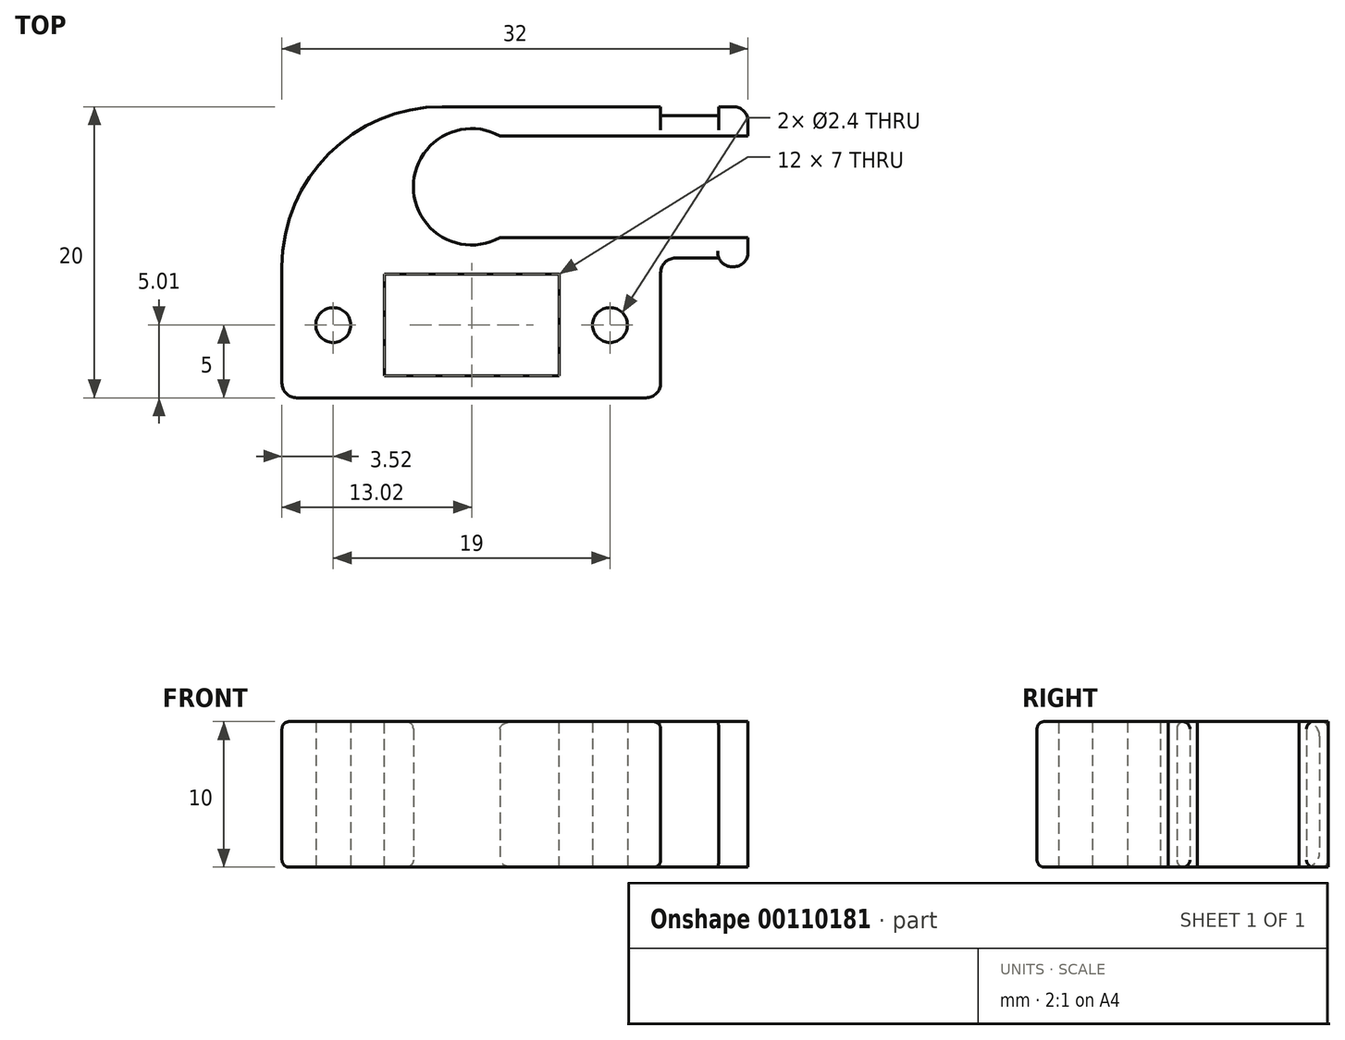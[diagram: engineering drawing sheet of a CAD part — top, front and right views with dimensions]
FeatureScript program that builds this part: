
annotation { "Feature Type Name" : "Feature", "Feature Type Description" : "" }
export const myFeature = defineFeature(function(context is Context, id is Id, definition is map)
    precondition{}
    {
        {
            var Q0;
            Q0=qCreatedBy(makeId("Top.planeOp"),FACE);
            var sketch = newSketch(context, id + "F0", { "sketchPlane" : qUnion([Q0])});
            skArc(sketch, "E0", {"start": v(-3.5, 1.94) * mm, "mid": v(-2.83, -2.83) * mm, "end": v(1.94, -3.5) * mm});
            skLineSegment(sketch, "E1.right", {"start": v(12.98, -5.5) * mm, "end": v(12.98, -14.5) * mm});
            skLineSegment(sketch, "E2.left", {"start": v(12.98, -14.5) * mm, "end": v(12.98, -5.5) * mm});
            skLineSegment(sketch, "E2.right", {"start": v(-13.02, -14.5) * mm, "end": v(-13.02, -4.5) * mm});
            skLineSegment(sketch, "E3", {"start": v(-13.02, -14.5) * mm, "end": v(12.98, -14.5) * mm});
            skLineSegment(sketch, "E4.bottom", {"start": v(-13.02, -14.5) * mm, "end": v(12.98, -14.5) * mm, "construction": true});
            skLineSegment(sketch, "E4.left", {"start": v(-13.02, -14.5) * mm, "end": v(-13.02, -9.5) * mm, "construction": true});
            skLineSegment(sketch, "E4.right", {"start": v(12.98, -14.5) * mm, "end": v(12.98, -9.7) * mm, "construction": true});
            skCircle(sketch, "E5", {"center": v(-9.5, -9.5) * mm, "radius": 1.2 * mm});
            skCircle(sketch, "E6", {"center": v(9.5, -9.5) * mm, "radius": 1.2 * mm});
            skArc(sketch, "E7", {"start": v(1.94, 3.5) * mm, "mid": v(-1.1, 3.84) * mm, "end": v(-3.5, 1.94) * mm});
            skLineSegment(sketch, "E8.top", {"start": v(-13.02, 5.5) * mm, "end": v(12.98, 5.5) * mm});
            skLineSegment(sketch, "E8.left", {"start": v(-13.02, -4.5) * mm, "end": v(-13.02, 5.5) * mm});
            skLineSegment(sketch, "E9.bottom", {"start": v(1.94, -3.5) * mm, "end": v(18.98, -3.5) * mm});
            skLineSegment(sketch, "E9.top", {"start": v(1.94, 3.5) * mm, "end": v(18.98, 3.5) * mm});
            skPoint(sketch, "E10.orphan", {"position": v(0, -3.5) * mm});
            skLineSegment(sketch, "E11.top", {"start": v(16.98, 5.5) * mm, "end": v(18.98, 5.5) * mm});
            skLineSegment(sketch, "E11.right", {"start": v(18.98, -5.5) * mm, "end": v(18.98, -3.5) * mm});
            skLineSegment(sketch, "E12.bottom", {"start": v(18.98, -3.5) * mm, "end": v(12.98, -3.5) * mm});
            skLineSegment(sketch, "E12.top", {"start": v(18.98, -5.5) * mm, "end": v(16.98, -5.5) * mm});
            skLineSegment(sketch, "E12.left", {"start": v(18.98, -3.5) * mm, "end": v(18.98, -5.5) * mm});
            skPoint(sketch, "E13.orphan", {"position": v(12.98, -4.9) * mm});
            skLineSegment(sketch, "E14.trimOffspring", {"start": v(18.98, 3.5) * mm, "end": v(18.98, 5.5) * mm});
            skPoint(sketch, "E15.orphan", {"position": v(0, -9.5) * mm});
            skLineSegment(sketch, "E16.top", {"start": v(12.98, -4.9) * mm, "end": v(16.98, -4.9) * mm});
            skLineSegment(sketch, "E16.left", {"start": v(12.98, -5.5) * mm, "end": v(12.98, -4.9) * mm});
            skLineSegment(sketch, "E16.right", {"start": v(16.98, -5.5) * mm, "end": v(16.98, -4.9) * mm});
            skLineSegment(sketch, "E17.top", {"start": v(12.98, 4.9) * mm, "end": v(16.98, 4.9) * mm});
            skLineSegment(sketch, "E17.left", {"start": v(12.98, 5.5) * mm, "end": v(12.98, 4.9) * mm});
            skLineSegment(sketch, "E17.right", {"start": v(16.98, 5.5) * mm, "end": v(16.98, 4.9) * mm});
            skSolve(sketch);
        }
        {
            var Q0;
            Q0 = qSketchRegion(id + "F0", true);
            extrude(context, id + "F1", {"entities" : qUnion([Q0]), "depth" : 10 * mm});
        }
        {
            var Q0;
            Q0=makeQuery(id+"F1.opExtrude","SWEPT_EDGE",EDGE,{"disambiguationData":[OSD([sQuery(id+"F0.wireOp",EDGE,"E11.top"),sQuery(id+"F0.wireOp",EDGE,"E14.trimOffspring")])]});
            var Q1;
            Q1=makeQuery(id+"F1.opExtrude","SWEPT_EDGE",EDGE,{"disambiguationData":[OSD([sQuery(id+"F0.wireOp",EDGE,"E12.top"),sQuery(id+"F0.wireOp",EDGE,"E12.left")])]});
            var Q2;
            Q2=makeQuery(id+"F1.opExtrude","CAP_EDGE",EDGE,{"disambiguationData":[OSD([sQuery(id+"F0.wireOp",EDGE,"E17.top")])],"isStart":false});
            var Q3;
            Q3=makeQuery(id+"F1.opExtrude","CAP_EDGE",EDGE,{"disambiguationData":[OSD([sQuery(id+"F0.wireOp",EDGE,"E17.top")])],"isStart":true});
            var Q4;
            Q4=makeQuery(id+"F1.opExtrude","SWEPT_EDGE",EDGE,{"disambiguationData":[OSD([sQuery(id+"F0.wireOp",EDGE,"E16.top"),sQuery(id+"F0.wireOp",EDGE,"E16.left")])]});
            var Q5;
            Q5=makeQuery(id+"F1.opExtrude","SWEPT_EDGE",EDGE,{"disambiguationData":[OSD([sQuery(id+"F0.wireOp",EDGE,"E3"),sQuery(id+"F0.wireOp",EDGE,"E2.left")])]});
            var Q6;
            Q6=makeQuery(id+"F1.opExtrude","SWEPT_EDGE",EDGE,{"disambiguationData":[OSD([sQuery(id+"F0.wireOp",EDGE,"E2.right"),sQuery(id+"F0.wireOp",EDGE,"E3")])]});
            fillet(context, id + "F2", {"entities" : qUnion([Q0, Q1, Q2, Q3, Q4, Q5, Q6]), "radius" : 1 * mm, "tangentPropagation" : true, "allowEdgeOverflow" : false});
        }
        {
            var Q0;
            Q0=makeQuery(id+"F1.opExtrude","SWEPT_EDGE",EDGE,{"disambiguationData":[OSD([sQuery(id+"F0.wireOp",EDGE,"E8.top"),sQuery(id+"F0.wireOp",EDGE,"E8.left")])]});
            fillet(context, id + "F3", {"entities" : qUnion([Q0]), "radius" : 11 * mm, "tangentPropagation" : true, "allowEdgeOverflow" : false});
        }
        {
            var Q0;
            Q0=makeQuery(id+"F1.opExtrude","CAP_FACE",FACE,{"disambiguationData":[OSD([sQuery(id+"F0.wireOp",EDGE,"E0"),sQuery(id+"F0.wireOp",EDGE,"E2.right"),sQuery(id+"F0.wireOp",EDGE,"E3"),sQuery(id+"F0.wireOp",EDGE,"E5"),sQuery(id+"F0.wireOp",EDGE,"E6"),sQuery(id+"F0.wireOp",EDGE,"E7"),sQuery(id+"F0.wireOp",EDGE,"E8.top"),sQuery(id+"F0.wireOp",EDGE,"E8.left"),sQuery(id+"F0.wireOp",EDGE,"E9.bottom"),sQuery(id+"F0.wireOp",EDGE,"E9.top"),sQuery(id+"F0.wireOp",EDGE,"E11.top"),sQuery(id+"F0.wireOp",EDGE,"E2.left"),sQuery(id+"F0.wireOp",EDGE,"E12.bottom"),sQuery(id+"F0.wireOp",EDGE,"E12.top"),sQuery(id+"F0.wireOp",EDGE,"E12.left"),sQuery(id+"F0.wireOp",EDGE,"E14.trimOffspring"),sQuery(id+"F0.wireOp",EDGE,"E16.top"),sQuery(id+"F0.wireOp",EDGE,"E16.left"),sQuery(id+"F0.wireOp",EDGE,"E16.right"),sQuery(id+"F0.wireOp",EDGE,"E17.top"),sQuery(id+"F0.wireOp",EDGE,"E17.left"),sQuery(id+"F0.wireOp",EDGE,"E17.right")])],"isStart":false});
            var sketch = newSketch(context, id + "F4", { "sketchPlane" : qUnion([Q0])});
            skLineSegment(sketch, "E18.bottom", {"start": v(6, -13) * mm, "end": v(-6, -13) * mm});
            skLineSegment(sketch, "E18.top", {"start": v(6, -6) * mm, "end": v(-6, -6) * mm});
            skLineSegment(sketch, "E18.left", {"start": v(6, -13) * mm, "end": v(6, -6) * mm});
            skLineSegment(sketch, "E18.right", {"start": v(-6, -13) * mm, "end": v(-6, -6) * mm});
            skPoint(sketch, "E18.middle", {"position": v(0, -9.5) * mm});
            skSolve(sketch);
        }
        {
            var Q0;
            Q0=makeQuery(id+"F4.imprint","IMPRINT",FACE,{"disambiguationData":[TD([[makeQuery(id+"F4.imprint","IMPRINT",EDGE,{"derivedFrom":sQuery(id+"F4.wireOp",EDGE,"E18.bottom")}),-1.0]])]});
            extrude(context, id + "F5", {"entities" : qUnion([Q0]), "operationType" : NewBodyOperationType.REMOVE, "oppositeDirection" : true, "depth" : 10 * mm});
        }
        {
            var Q0;
            {var subQ0=sQuery(id+"F0.wireOp",EDGE,"E8.left");var subQ1=sQuery(id+"F0.wireOp",EDGE,"E8.top");Q0=makeQuery(id+"F3.opFillet","BLEND_EDGE",EDGE,{"blendedFrom":[makeQuery(id+"F1.opExtrude","SWEPT_EDGE",EDGE,{"disambiguationData":[OSD([subQ1,subQ0])]}),makeQuery(id+"F1.opExtrude","CAP_FACE",FACE,{"disambiguationData":[OSD([sQuery(id+"F0.wireOp",EDGE,"E0"),sQuery(id+"F0.wireOp",EDGE,"E2.right"),sQuery(id+"F0.wireOp",EDGE,"E3"),sQuery(id+"F0.wireOp",EDGE,"E5"),sQuery(id+"F0.wireOp",EDGE,"E6"),sQuery(id+"F0.wireOp",EDGE,"E7"),subQ1,subQ0,sQuery(id+"F0.wireOp",EDGE,"E9.bottom"),sQuery(id+"F0.wireOp",EDGE,"E9.top"),sQuery(id+"F0.wireOp",EDGE,"E11.top"),sQuery(id+"F0.wireOp",EDGE,"E2.left"),sQuery(id+"F0.wireOp",EDGE,"E12.bottom"),sQuery(id+"F0.wireOp",EDGE,"E12.top"),sQuery(id+"F0.wireOp",EDGE,"E12.left"),sQuery(id+"F0.wireOp",EDGE,"E14.trimOffspring"),sQuery(id+"F0.wireOp",EDGE,"E16.top"),sQuery(id+"F0.wireOp",EDGE,"E16.left"),sQuery(id+"F0.wireOp",EDGE,"E16.right"),sQuery(id+"F0.wireOp",EDGE,"E17.top"),sQuery(id+"F0.wireOp",EDGE,"E17.left"),sQuery(id+"F0.wireOp",EDGE,"E17.right")])],"isStart":false})],"blendedInto":[makeQuery(id+"F1.opExtrude","CAP_FACE",FACE,{"disambiguationData":[OSD([sQuery(id+"F0.wireOp",EDGE,"E0"),sQuery(id+"F0.wireOp",EDGE,"E2.right"),sQuery(id+"F0.wireOp",EDGE,"E3"),sQuery(id+"F0.wireOp",EDGE,"E5"),sQuery(id+"F0.wireOp",EDGE,"E6"),sQuery(id+"F0.wireOp",EDGE,"E7"),subQ1,subQ0,sQuery(id+"F0.wireOp",EDGE,"E9.bottom"),sQuery(id+"F0.wireOp",EDGE,"E9.top"),sQuery(id+"F0.wireOp",EDGE,"E11.top"),sQuery(id+"F0.wireOp",EDGE,"E2.left"),sQuery(id+"F0.wireOp",EDGE,"E12.bottom"),sQuery(id+"F0.wireOp",EDGE,"E12.top"),sQuery(id+"F0.wireOp",EDGE,"E12.left"),sQuery(id+"F0.wireOp",EDGE,"E14.trimOffspring"),sQuery(id+"F0.wireOp",EDGE,"E16.top"),sQuery(id+"F0.wireOp",EDGE,"E16.left"),sQuery(id+"F0.wireOp",EDGE,"E16.right"),sQuery(id+"F0.wireOp",EDGE,"E17.top"),sQuery(id+"F0.wireOp",EDGE,"E17.left"),sQuery(id+"F0.wireOp",EDGE,"E17.right")])],"isStart":false})]});}
            var Q1;
            {var subQ0=sQuery(id+"F0.wireOp",EDGE,"E8.left");var subQ1=sQuery(id+"F0.wireOp",EDGE,"E8.top");Q1=makeQuery(id+"F3.opFillet","BLEND_EDGE",EDGE,{"blendedFrom":[makeQuery(id+"F1.opExtrude","SWEPT_EDGE",EDGE,{"disambiguationData":[OSD([subQ1,subQ0])]}),makeQuery(id+"F1.opExtrude","CAP_FACE",FACE,{"disambiguationData":[OSD([sQuery(id+"F0.wireOp",EDGE,"E0"),sQuery(id+"F0.wireOp",EDGE,"E2.right"),sQuery(id+"F0.wireOp",EDGE,"E3"),sQuery(id+"F0.wireOp",EDGE,"E5"),sQuery(id+"F0.wireOp",EDGE,"E6"),sQuery(id+"F0.wireOp",EDGE,"E7"),subQ1,subQ0,sQuery(id+"F0.wireOp",EDGE,"E9.bottom"),sQuery(id+"F0.wireOp",EDGE,"E9.top"),sQuery(id+"F0.wireOp",EDGE,"E11.top"),sQuery(id+"F0.wireOp",EDGE,"E2.left"),sQuery(id+"F0.wireOp",EDGE,"E12.bottom"),sQuery(id+"F0.wireOp",EDGE,"E12.top"),sQuery(id+"F0.wireOp",EDGE,"E12.left"),sQuery(id+"F0.wireOp",EDGE,"E14.trimOffspring"),sQuery(id+"F0.wireOp",EDGE,"E16.top"),sQuery(id+"F0.wireOp",EDGE,"E16.left"),sQuery(id+"F0.wireOp",EDGE,"E16.right"),sQuery(id+"F0.wireOp",EDGE,"E17.top"),sQuery(id+"F0.wireOp",EDGE,"E17.left"),sQuery(id+"F0.wireOp",EDGE,"E17.right")])],"isStart":true})],"blendedInto":[makeQuery(id+"F1.opExtrude","CAP_FACE",FACE,{"disambiguationData":[OSD([sQuery(id+"F0.wireOp",EDGE,"E0"),sQuery(id+"F0.wireOp",EDGE,"E2.right"),sQuery(id+"F0.wireOp",EDGE,"E3"),sQuery(id+"F0.wireOp",EDGE,"E5"),sQuery(id+"F0.wireOp",EDGE,"E6"),sQuery(id+"F0.wireOp",EDGE,"E7"),subQ1,subQ0,sQuery(id+"F0.wireOp",EDGE,"E9.bottom"),sQuery(id+"F0.wireOp",EDGE,"E9.top"),sQuery(id+"F0.wireOp",EDGE,"E11.top"),sQuery(id+"F0.wireOp",EDGE,"E2.left"),sQuery(id+"F0.wireOp",EDGE,"E12.bottom"),sQuery(id+"F0.wireOp",EDGE,"E12.top"),sQuery(id+"F0.wireOp",EDGE,"E12.left"),sQuery(id+"F0.wireOp",EDGE,"E14.trimOffspring"),sQuery(id+"F0.wireOp",EDGE,"E16.top"),sQuery(id+"F0.wireOp",EDGE,"E16.left"),sQuery(id+"F0.wireOp",EDGE,"E16.right"),sQuery(id+"F0.wireOp",EDGE,"E17.top"),sQuery(id+"F0.wireOp",EDGE,"E17.left"),sQuery(id+"F0.wireOp",EDGE,"E17.right")])],"isStart":true})]});}
            var Q2;
            Q2=makeQuery(id+"F1.opExtrude","CAP_EDGE",EDGE,{"disambiguationData":[OSD([sQuery(id+"F0.wireOp",EDGE,"E0"),sQuery(id+"F0.wireOp",EDGE,"E7")])],"isStart":true});
            var Q3;
            Q3=makeQuery(id+"F1.opExtrude","CAP_EDGE",EDGE,{"disambiguationData":[OSD([sQuery(id+"F0.wireOp",EDGE,"E0"),sQuery(id+"F0.wireOp",EDGE,"E7")])],"isStart":false});
            fillet(context, id + "F6", {"entities" : qUnion([Q0, Q1, Q2, Q3]), "radius" : 0.5 * mm, "tangentPropagation" : true, "allowEdgeOverflow" : false});
        }
    });
